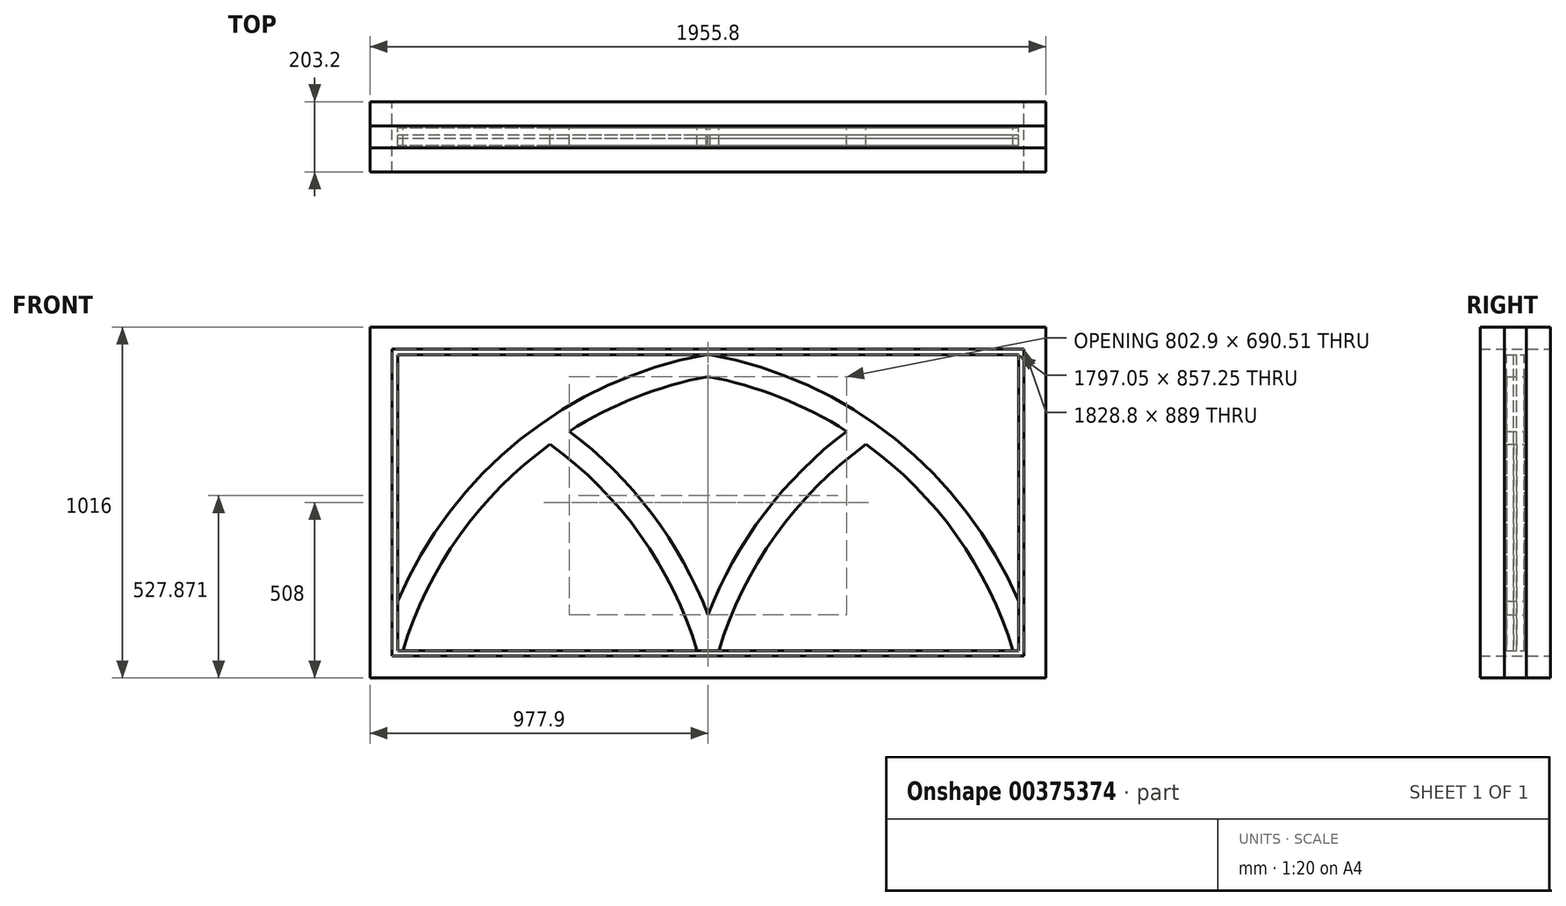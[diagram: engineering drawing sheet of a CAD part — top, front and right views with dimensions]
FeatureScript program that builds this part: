
annotation { "Feature Type Name" : "Feature", "Feature Type Description" : "" }
export const myFeature = defineFeature(function(context is Context, id is Id, definition is map)
    precondition{}
    {
        {
            var Q0;
            Q0=qCreatedBy(makeId("Front.planeOp"),FACE);
            var sketch = newSketch(context, id + "F0", { "sketchPlane" : qUnion([Q0])});
            skLineSegment(sketch, "E0.bottom", {"start": v(914.4, -444.5) * mm, "end": v(-914.4, -444.5) * mm});
            skLineSegment(sketch, "E0.top", {"start": v(914.4, 444.5) * mm, "end": v(-914.4, 444.5) * mm});
            skLineSegment(sketch, "E0.left", {"start": v(914.4, -444.5) * mm, "end": v(914.4, 444.5) * mm});
            skLineSegment(sketch, "E0.right", {"start": v(-914.4, -444.5) * mm, "end": v(-914.4, 444.5) * mm});
            skPoint(sketch, "E0.middle", {"position": v(0, 0) * mm});
            skLineSegment(sketch, "E1.0", {"start": v(898.52, 428.63) * mm, "end": v(-898.52, 428.62) * mm});
            skLineSegment(sketch, "E1.1", {"start": v(898.52, -428.63) * mm, "end": v(898.52, 428.63) * mm});
            skLineSegment(sketch, "E1.2", {"start": v(898.52, -428.62) * mm, "end": v(-457.2, -428.63) * mm});
            skLineSegment(sketch, "E1.3", {"start": v(-898.52, -428.62) * mm, "end": v(-898.52, 428.62) * mm});
            skLineSegment(sketch, "E2.0", {"start": v(977.9, 508) * mm, "end": v(-977.9, 508) * mm});
            skLineSegment(sketch, "E2.1", {"start": v(977.9, -508) * mm, "end": v(977.9, 508) * mm});
            skLineSegment(sketch, "E2.2", {"start": v(977.9, -508) * mm, "end": v(-977.9, -508) * mm});
            skLineSegment(sketch, "E2.3", {"start": v(-977.9, -508) * mm, "end": v(-977.9, 508) * mm});
            skLineSegment(sketch, "E3", {"start": v(0, 0) * mm, "end": v(0, 763.34) * mm, "construction": true});
            skPoint(sketch, "E3.endSnap0", {"position": v(0, 508) * mm});
            skLineSegment(sketch, "E4", {"start": v(0, 0) * mm, "end": v(0, -916.59) * mm, "construction": true});
            skPoint(sketch, "E4.endSnap0", {"position": v(0, -508) * mm});
            skLineSegment(sketch, "E5", {"start": v(1104.7, 0) * mm, "end": v(-1280.95, 0) * mm, "construction": true});
            skLineSegment(sketch, "E6.0", {"start": v(31.75, 428.63) * mm, "end": v(31.75, -706.28) * mm, "construction": true});
            skLineSegment(sketch, "E7.0", {"start": v(-31.75, 428.63) * mm, "end": v(-31.75, -706.28) * mm, "construction": true});
            skLineSegment(sketch, "E8.0", {"start": v(-47.62, 0) * mm, "end": v(-47.62, -706.28) * mm, "construction": true});
            skLineSegment(sketch, "E9.0", {"start": v(-866.78, -428.63) * mm, "end": v(-866.78, 428.62) * mm, "construction": true});
            skLineSegment(sketch, "E10.0", {"start": v(898.52, -396.88) * mm, "end": v(-914.4, -396.88) * mm, "construction": true});
            skLineSegment(sketch, "E11", {"start": v(-765.88, 365.12) * mm, "end": v(-1161.07, 365.12) * mm, "construction": true});
            skArc(sketch, "E12.MirrorCS", {"start": v(-870.67, 427.49) * mm, "mid": v(-868.73, 429.83) * mm, "end": v(-866.77, 432.16) * mm});
            skLineSegment(sketch, "E13", {"start": v(-173.05, 365.12) * mm, "end": v(209.25, 365.13) * mm, "construction": true});
            skLineSegment(sketch, "E14", {"start": v(977.9, -916.59) * mm, "end": v(977.9, -508) * mm, "construction": true});
            skPoint(sketch, "E15.orphan", {"position": v(0, -706.28) * mm});
            skLineSegment(sketch, "E16", {"start": v(0, -916.59) * mm, "end": v(977.9, -916.59) * mm, "construction": true});
            skLineSegment(sketch, "E17", {"start": v(-914.4, -396.88) * mm, "end": v(-977.9, -396.88) * mm, "construction": true});
            skLineSegment(sketch, "E18", {"start": v(-946.15, -396.88) * mm, "end": v(-946.15, -916.59) * mm, "construction": true});
            skLineSegment(sketch, "E19", {"start": v(-946.15, -916.59) * mm, "end": v(0, -916.59) * mm, "construction": true});
            skLineSegment(sketch, "E20", {"start": v(-914.4, -444.5) * mm, "end": v(-914.4, -832.27) * mm, "construction": true});
            skLineSegment(sketch, "E21", {"start": v(-914.4, -832.27) * mm, "end": v(0, -832.27) * mm, "construction": true});
            skLineSegment(sketch, "E22", {"start": v(-457.2, -832.27) * mm, "end": v(-457.2, 168.66) * mm, "construction": true});
            skLineSegment(sketch, "E23", {"start": v(-914.4, -638.38) * mm, "end": v(-882.65, -638.38) * mm, "construction": true});
            skLineSegment(sketch, "E24", {"start": v(-882.65, -638.38) * mm, "end": v(-882.65, -342.4) * mm, "construction": true});
            skArc(sketch, "E25", {"start": v(0, 365.13) * mm, "mid": v(-208.28, 304.92) * mm, "end": v(-401.45, 206.46) * mm});
            skArc(sketch, "E26.MirrorCS", {"start": v(-914.4, 365.12) * mm, "mid": v(-890.53, 360.36) * mm, "end": v(-866.78, 355.09) * mm});
            skArc(sketch, "E27.0", {"start": v(-5.86, 428.63) * mm, "mid": v(-542.25, 183.73) * mm, "end": v(-898.53, -286.13) * mm});
            skArc(sketch, "E28.0", {"start": v(-902.63, 427.52) * mm, "mid": v(-884.68, 424) * mm, "end": v(-866.78, 420.2) * mm});
            skArc(sketch, "E29.trimOffspring", {"start": v(-457.2, 168.66) * mm, "mid": v(-195.27, -94.94) * mm, "end": v(-31.75, -428.62) * mm});
            skArc(sketch, "E30.trimOffspring", {"start": v(-401.45, 206.46) * mm, "mid": v(-163.28, -31.2) * mm, "end": v(0, -325.38) * mm});
            skArc(sketch, "E31.trimOffspring", {"start": v(-457.2, 168.66) * mm, "mid": v(-719.13, -94.94) * mm, "end": v(-882.65, -428.62) * mm});
            skArc(sketch, "E32.MirrorCS", {"start": v(0, 365.13) * mm, "mid": v(208.28, 304.92) * mm, "end": v(401.45, 206.46) * mm});
            skArc(sketch, "E33.MirrorCS", {"start": v(5.86, 428.63) * mm, "mid": v(542.25, 183.73) * mm, "end": v(898.52, -286.13) * mm});
            skArc(sketch, "E34.MirrorCS", {"start": v(457.2, 168.66) * mm, "mid": v(719.13, -94.94) * mm, "end": v(882.65, -428.62) * mm});
            skArc(sketch, "E35.MirrorCS", {"start": v(457.2, 168.66) * mm, "mid": v(195.27, -94.94) * mm, "end": v(31.75, -428.62) * mm});
            skArc(sketch, "E36.MirrorCS", {"start": v(401.45, 206.46) * mm, "mid": v(163.28, -31.2) * mm, "end": v(0, -325.38) * mm});
            skPoint(sketch, "E37.orphan", {"position": v(-11.77, 427.52) * mm});
            skPoint(sketch, "E38.orphan", {"position": v(11.77, 427.52) * mm});
            skPoint(sketch, "E39.trimOffspring.end.orphan", {"position": v(-29.06, -410.32) * mm});
            skPoint(sketch, "E40.trimOffspring.end.orphan", {"position": v(29.06, -410.32) * mm});
            skLineSegment(sketch, "E41", {"start": v(-457.2, -428.63) * mm, "end": v(-898.52, -428.63) * mm});
            skSolve(sketch);
        }
        {
            var Q0;
            {var subQ1=sQuery(id+"F0.wireOp",EDGE,"E0.bottom");Q0=makeQuery(id+"F0.imprint","IMPRINT",FACE,{"disambiguationData":[TD([[makeQuery(id+"F0.imprint","IMPRINT",EDGE,{"derivedFrom":subQ1}),1.0]])]});}
            extrude(context, id + "F1", {"entities" : qUnion([Q0]), "endBound" : BoundingType.SYMMETRIC, "depth" : 203.2 * mm});
        }
        {
            var Q0;
            Q0 = qSketchRegion(id + "F0", true);
            var Q1;
            {var subQ16=sQuery(id+"F0.wireOp",EDGE,"E0.bottom");Q1=makeQuery(id+"F0.imprint","IMPRINT",FACE,{"disambiguationData":[TD([[makeQuery(id+"F0.imprint","IMPRINT",EDGE,{"derivedFrom":subQ16}),-1.0]])]});}
            extrude(context, id + "F2", {"entities" : qUnion([Q0, Q1]), "endBound" : BoundingType.SYMMETRIC, "depth" : 63.5 * mm});
        }
        {
            var Q0;
            {var subQ0=sQuery(id+"F0.wireOp",EDGE,"E27.0");Q0=makeQuery(id+"F0.imprint","IMPRINT",FACE,{"disambiguationData":[TD([[makeQuery(id+"F0.imprint","IMPRINT",EDGE,{"derivedFrom":subQ0}),-1.0]])]});}
            var Q1;
            {var subQ3=sQuery(id+"F0.wireOp",EDGE,"E29.trimOffspring");Q1=makeQuery(id+"F0.imprint","IMPRINT",FACE,{"disambiguationData":[TD([[makeQuery(id+"F0.imprint","IMPRINT",EDGE,{"derivedFrom":subQ3}),-1.0]])]});}
            var Q2;
            {var subQ0=sQuery(id+"F0.wireOp",EDGE,"E34.MirrorCS");Q2=makeQuery(id+"F0.imprint","IMPRINT",FACE,{"disambiguationData":[TD([[makeQuery(id+"F0.imprint","IMPRINT",EDGE,{"derivedFrom":subQ0}),-1.0]])]});}
            var Q3;
            Q3=makeQuery(id+"F0.imprint","IMPRINT",FACE,{"disambiguationData":[TD([[makeQuery(id+"F0.imprint","IMPRINT",EDGE,{"derivedFrom":sQuery(id+"F0.wireOp",EDGE,"E25")}),1.0]])]});
            var Q4;
            {var subQ3=sQuery(id+"F0.wireOp",EDGE,"E33.MirrorCS");Q4=makeQuery(id+"F0.imprint","IMPRINT",FACE,{"disambiguationData":[TD([[makeQuery(id+"F0.imprint","IMPRINT",EDGE,{"derivedFrom":subQ3}),1.0]])]});}
            extrude(context, id + "F3", {"entities" : qUnion([Q0, Q1, Q2, Q3, Q4]), "endBound" : BoundingType.SYMMETRIC, "depth" : 9.52 * mm});
        }
        {
            var Q0;
            Q0=makeQuery(id+"F0.imprint","IMPRINT",FACE,{"disambiguationData":[TD([[makeQuery(id+"F0.imprint","IMPRINT",EDGE,{"derivedFrom":sQuery(id+"F0.wireOp",EDGE,"E25")}),-1.0]])]});
            extrude(context, id + "F4", {"entities" : qUnion([Q0]), "endBound" : BoundingType.SYMMETRIC, "depth" : 50.8 * mm});
        }
    });
